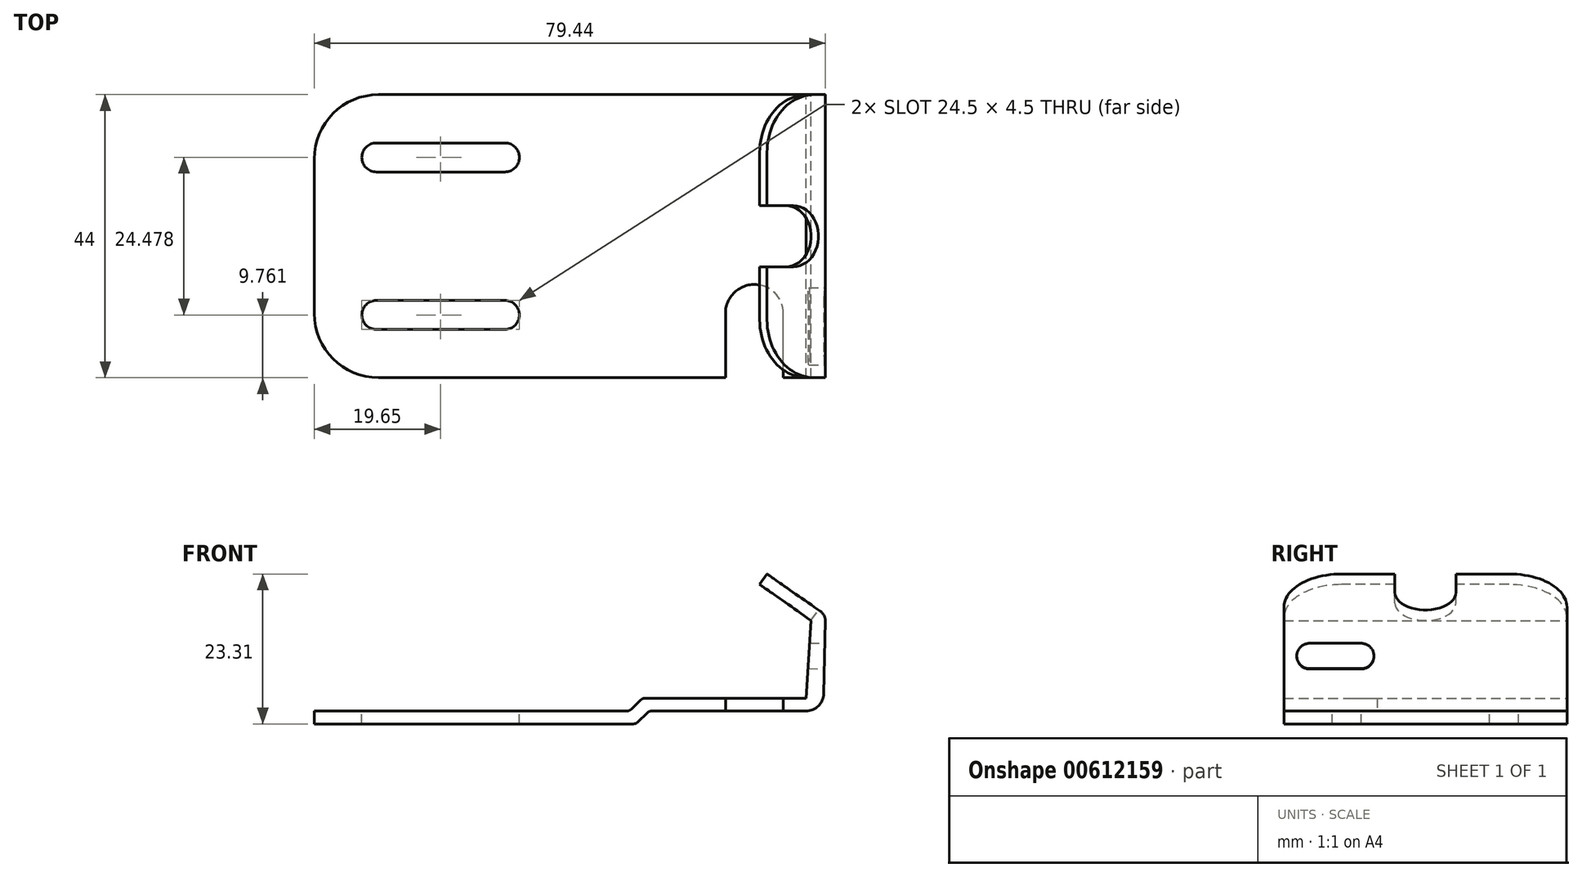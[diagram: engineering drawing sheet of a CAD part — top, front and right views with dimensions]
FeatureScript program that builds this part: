
annotation { "Feature Type Name" : "Feature", "Feature Type Description" : "" }
export const myFeature = defineFeature(function(context is Context, id is Id, definition is map)
    precondition{}
    {
        {
            var Q0;
            Q0=qCreatedBy(makeId("Front.planeOp"),FACE);
            var sketch = newSketch(context, id + "F0", { "sketchPlane" : qUnion([Q0])});
            skLineSegment(sketch, "E0", {"start": v(-0.4, 0) * mm, "end": v(-40, 0) * mm});
            skLineSegment(sketch, "E1", {"start": v(-40, 0) * mm, "end": v(-40, 2) * mm});
            skLineSegment(sketch, "E2", {"start": v(-40, 2) * mm, "end": v(-1.43, 2) * mm});
            skLineSegment(sketch, "E3", {"start": v(-0.73, 2.28) * mm, "end": v(0.75, 3.72) * mm});
            skLineSegment(sketch, "E4", {"start": v(1.44, 4) * mm, "end": v(26.44, 4) * mm});
            skLineSegment(sketch, "E5", {"start": v(0.3, 0.28) * mm, "end": v(1.77, 1.72) * mm});
            skLineSegment(sketch, "E6", {"start": v(2.46, 2) * mm, "end": v(26.44, 2) * mm});
            skPoint(sketch, "E7.visualSharp", {"position": v(-1.02, 2) * mm});
            skArc(sketch, "E7.filletArc", {"start": v(-1.43, 2) * mm, "mid": v(-1.05, 2.07) * mm, "end": v(-0.73, 2.28) * mm});
            skPoint(sketch, "E8.visualSharp", {"position": v(1.04, 4) * mm});
            skArc(sketch, "E8.filletArc", {"start": v(1.44, 4) * mm, "mid": v(1.07, 3.93) * mm, "end": v(0.75, 3.72) * mm});
            skPoint(sketch, "E9.visualSharp", {"position": v(2.06, 2) * mm});
            skArc(sketch, "E9.filletArc", {"start": v(2.46, 2) * mm, "mid": v(2.09, 1.93) * mm, "end": v(1.77, 1.72) * mm});
            skPoint(sketch, "E10.visualSharp", {"position": v(0, 0) * mm});
            skArc(sketch, "E10.filletArc", {"start": v(-0.4, 0) * mm, "mid": v(-0.03, 0.07) * mm, "end": v(0.3, 0.28) * mm});
            skArc(sketch, "E11", {"start": v(26.44, 2) * mm, "mid": v(28.38, 2.79) * mm, "end": v(29.2, 4.7) * mm});
            skLineSegment(sketch, "E12", {"start": v(29.2, 4.7) * mm, "end": v(29.44, 16.03) * mm});
            skArc(sketch, "E13", {"start": v(29.44, 16.03) * mm, "mid": v(29.26, 16.85) * mm, "end": v(28.7, 17.5) * mm});
            skLineSegment(sketch, "E14", {"start": v(28.7, 17.5) * mm, "end": v(27.76, 18.15) * mm});
            skLineSegment(sketch, "E15", {"start": v(27.76, 18.15) * mm, "end": v(26.61, 16.51) * mm});
            skLineSegment(sketch, "E16", {"start": v(26.61, 16.51) * mm, "end": v(27.25, 16.06) * mm});
            skLineSegment(sketch, "E17", {"start": v(27.25, 16.06) * mm, "end": v(26.44, 4) * mm});
            skSolve(sketch);
        }
        {
            var Q0;
            Q0=makeQuery(id+"F0.imprint","IMPRINT",FACE,{"disambiguationData":[TD([[makeQuery(id+"F0.imprint","IMPRINT",EDGE,{"derivedFrom":sQuery(id+"F0.wireOp",EDGE,"E0")}),-1.0]])]});
            extrude(context, id + "F1", {"entities" : qUnion([Q0]), "endBound" : BoundingType.SYMMETRIC, "depth" : 44 * mm, "offsetDistance" : 25 * mm});
        }
        {
            var Q0;
            Q0=makeQuery(id+"F1.opExtrude","SWEPT_FACE",FACE,{"disambiguationData":[OSD([sQuery(id+"F0.wireOp",EDGE,"E2")])]});
            var sketch = newSketch(context, id + "F2", { "sketchPlane" : qUnion([Q0])});
            skLineSegment(sketch, "E18", {"start": v(-50, -12) * mm, "end": v(-50, 12) * mm});
            skArc(sketch, "E19", {"start": v(-50, -12) * mm, "mid": v(-47.07, -19.07) * mm, "end": v(-40, -22) * mm});
            skArc(sketch, "E20", {"start": v(-50, 12) * mm, "mid": v(-47.07, 19.07) * mm, "end": v(-40, 22) * mm});
            skSolve(sketch);
        }
        {
            var Q0;
            Q0=makeQuery(id+"F2.imprint","IMPRINT",FACE,{"disambiguationData":[TD([[makeQuery(id+"F2.imprint","IMPRINT",EDGE,{"derivedFrom":sQuery(id+"F2.wireOp",EDGE,"E18")}),-1.0]])]});
            extrude(context, id + "F3", {"entities" : qUnion([Q0]), "operationType" : NewBodyOperationType.ADD, "oppositeDirection" : true, "depth" : 2 * mm, "offsetDistance" : 25 * mm});
        }
        {
            var Q0;
            {var subQ0=sQuery(id+"F0.wireOp",EDGE,"E2");Q0=makeQuery(id+"F3.boolean.opBoolean","MERGE",FACE,{"derivedFrom":[makeQuery(id+"F1.opExtrude","SWEPT_FACE",FACE,{"disambiguationData":[OSD([subQ0])]}),makeQuery(id+"F3.opExtrude","CAP_FACE",FACE,{"disambiguationData":[OSD([sQuery(id+"F0.wireOp",EDGE,"E1"),subQ0,sQuery(id+"F2.wireOp",EDGE,"E18"),sQuery(id+"F2.wireOp",EDGE,"E19"),sQuery(id+"F2.wireOp",EDGE,"E20")])],"isStart":true})]});}
            var sketch = newSketch(context, id + "F4", { "sketchPlane" : qUnion([Q0])});
            skLineSegment(sketch, "E21.bottom", {"start": v(-40.35, 9.99) * mm, "end": v(-20.35, 9.99) * mm});
            skLineSegment(sketch, "E21.top", {"start": v(-40.35, 14.49) * mm, "end": v(-20.35, 14.49) * mm});
            skArc(sketch, "E22", {"start": v(-40.35, 14.49) * mm, "mid": v(-42.6, 12.24) * mm, "end": v(-40.35, 9.99) * mm});
            skArc(sketch, "E23", {"start": v(-20.35, 9.99) * mm, "mid": v(-18.1, 12.24) * mm, "end": v(-20.35, 14.49) * mm});
            skLineSegment(sketch, "E24.MirrorCS", {"start": v(-40.35, -9.99) * mm, "end": v(-20.35, -9.99) * mm});
            skArc(sketch, "E25.MirrorCS", {"start": v(-40.35, -14.49) * mm, "mid": v(-42.6, -12.24) * mm, "end": v(-40.35, -9.99) * mm});
            skLineSegment(sketch, "E26.MirrorCS", {"start": v(-40.35, -14.49) * mm, "end": v(-20.35, -14.49) * mm});
            skArc(sketch, "E27.MirrorCS", {"start": v(-20.35, -9.99) * mm, "mid": v(-18.1, -12.24) * mm, "end": v(-20.35, -14.49) * mm});
            skSolve(sketch);
        }
        {
            var Q0;
            Q0 = qSketchRegion(id + "F4", true);
            var Q1;
            Q1=makeQuery(id+"F3.boolean.opBoolean","MERGE",FACE,{"derivedFrom":[makeQuery(id+"F1.opExtrude","SWEPT_FACE",FACE,{"disambiguationData":[OSD([sQuery(id+"F0.wireOp",EDGE,"E0")])]}),makeQuery(id+"F3.opExtrude","CAP_FACE",FACE,{"disambiguationData":[OSD([sQuery(id+"F0.wireOp",EDGE,"E1"),sQuery(id+"F0.wireOp",EDGE,"E2"),sQuery(id+"F2.wireOp",EDGE,"E18"),sQuery(id+"F2.wireOp",EDGE,"E19"),sQuery(id+"F2.wireOp",EDGE,"E20")])],"isStart":false})]});
            extrude(context, id + "F5", {"entities" : qUnion([Q0]), "operationType" : NewBodyOperationType.REMOVE, "endBound" : BoundingType.UP_TO_SURFACE, "oppositeDirection" : true, "depth" : 25 * mm, "endBoundEntityFace" : qUnion([Q1]), "offsetDistance" : 25 * mm});
        }
        {
            var Q0;
            Q0=makeQuery(id+"F1.opExtrude","SWEPT_FACE",FACE,{"disambiguationData":[OSD([sQuery(id+"F0.wireOp",EDGE,"E12")])]});
            var sketch = newSketch(context, id + "F6", { "sketchPlane" : qUnion([Q0])});
            skLineSegment(sketch, "E28.bottom", {"start": v(-18, 13.15) * mm, "end": v(-10, 13.15) * mm});
            skLineSegment(sketch, "E28.top", {"start": v(-18, 9.15) * mm, "end": v(-10, 9.15) * mm});
            skArc(sketch, "E29", {"start": v(-10, 9.15) * mm, "mid": v(-8, 11.15) * mm, "end": v(-10, 13.15) * mm});
            skArc(sketch, "E30", {"start": v(-18, 13.15) * mm, "mid": v(-20, 11.15) * mm, "end": v(-18, 9.15) * mm});
            skSolve(sketch);
        }
        {
            var Q0;
            Q0 = qSketchRegion(id + "F6", true);
            var Q1;
            Q1=makeQuery(id+"F1.opExtrude","SWEPT_FACE",FACE,{"disambiguationData":[OSD([sQuery(id+"F0.wireOp",EDGE,"E17")])]});
            extrude(context, id + "F7", {"entities" : qUnion([Q0]), "operationType" : NewBodyOperationType.REMOVE, "endBound" : BoundingType.UP_TO_SURFACE, "oppositeDirection" : true, "depth" : 25 * mm, "endBoundEntityFace" : qUnion([Q1]), "offsetDistance" : 25 * mm});
        }
        {
            var Q0;
            Q0=makeQuery(id+"F1.opExtrude","SWEPT_FACE",FACE,{"disambiguationData":[OSD([sQuery(id+"F0.wireOp",EDGE,"E14")])]});
            var sketch = newSketch(context, id + "F8", { "sketchPlane" : qUnion([Q0])});
            skLineSegment(sketch, "E31", {"start": v(3.33, -13) * mm, "end": v(3.33, 13) * mm});
            skArc(sketch, "E32", {"start": v(3.33, -13) * mm, "mid": v(5.97, -19.36) * mm, "end": v(12.33, -22) * mm});
            skArc(sketch, "E33", {"start": v(3.33, 13) * mm, "mid": v(5.97, 19.36) * mm, "end": v(12.33, 22) * mm});
            skSolve(sketch);
        }
        {
            var Q0;
            Q0=makeQuery(id+"F8.imprint","IMPRINT",FACE,{"disambiguationData":[TD([[makeQuery(id+"F8.imprint","IMPRINT",EDGE,{"derivedFrom":sQuery(id+"F8.wireOp",EDGE,"E31")}),-1.0]])]});
            var Q1;
            Q1=makeQuery(id+"F1.opExtrude","SWEPT_FACE",FACE,{"disambiguationData":[OSD([sQuery(id+"F0.wireOp",EDGE,"E16")])]});
            extrude(context, id + "F9", {"entities" : qUnion([Q0]), "operationType" : NewBodyOperationType.ADD, "endBound" : BoundingType.UP_TO_SURFACE, "oppositeDirection" : true, "depth" : 25 * mm, "endBoundEntityFace" : qUnion([Q1]), "offsetDistance" : 25 * mm});
        }
        {
            var Q0;
            {var subQ0=sQuery(id+"F0.wireOp",EDGE,"E14");Q0=makeQuery(id+"F9.boolean.opBoolean","MERGE",FACE,{"derivedFrom":[makeQuery(id+"F1.opExtrude","SWEPT_FACE",FACE,{"disambiguationData":[OSD([subQ0])]}),makeQuery(id+"F9.opExtrude","CAP_FACE",FACE,{"disambiguationData":[OSD([subQ0,sQuery(id+"F0.wireOp",EDGE,"E15"),sQuery(id+"F8.wireOp",EDGE,"E31"),sQuery(id+"F8.wireOp",EDGE,"E32"),sQuery(id+"F8.wireOp",EDGE,"E33")])],"isStart":true})]});}
            var sketch = newSketch(context, id + "F10", { "sketchPlane" : qUnion([Q0])});
            skLineSegment(sketch, "E34", {"start": v(3.33, 0) * mm, "end": v(13.48, 0) * mm, "construction": true});
            skLineSegment(sketch, "E35", {"start": v(3.33, -4.75) * mm, "end": v(8.33, -4.75) * mm});
            skLineSegment(sketch, "E36", {"start": v(3.33, 4.75) * mm, "end": v(8.33, 4.75) * mm});
            skArc(sketch, "E37", {"start": v(8.33, -4.75) * mm, "mid": v(13.08, 0) * mm, "end": v(8.33, 4.75) * mm});
            skSolve(sketch);
        }
        {
            var Q0;
            {var subQ0=sQuery(id+"F10.wireOp",EDGE,"E35");Q0=makeQuery(id+"F10.imprint","IMPRINT",FACE,{"disambiguationData":[TD([[makeQuery(id+"F10.imprint","IMPRINT",EDGE,{"derivedFrom":subQ0}),1.0]])]});}
            var Q1;
            Q1=makeQuery(id+"F9.boolean.opBoolean","MERGE",FACE,{"derivedFrom":[makeQuery(id+"F1.opExtrude","SWEPT_FACE",FACE,{"disambiguationData":[OSD([sQuery(id+"F0.wireOp",EDGE,"E16")])]}),makeQuery(id+"F9.opExtrude","CAP_FACE",FACE,{"disambiguationData":[OSD([sQuery(id+"F0.wireOp",EDGE,"E14"),sQuery(id+"F0.wireOp",EDGE,"E15"),sQuery(id+"F8.wireOp",EDGE,"E31"),sQuery(id+"F8.wireOp",EDGE,"E32"),sQuery(id+"F8.wireOp",EDGE,"E33")])],"isStart":false})]});
            extrude(context, id + "F11", {"entities" : qUnion([Q0]), "operationType" : NewBodyOperationType.REMOVE, "endBound" : BoundingType.UP_TO_SURFACE, "oppositeDirection" : true, "depth" : 25 * mm, "endBoundEntityFace" : qUnion([Q1]), "offsetDistance" : 25 * mm});
        }
        {
            var Q0;
            Q0=makeQuery(id+"F1.opExtrude","SWEPT_FACE",FACE,{"disambiguationData":[OSD([sQuery(id+"F0.wireOp",EDGE,"E6")])]});
            var sketch = newSketch(context, id + "F12", { "sketchPlane" : qUnion([Q0])});
            skLineSegment(sketch, "E38.bottom", {"start": v(22.92, 22) * mm, "end": v(13.92, 22) * mm});
            skLineSegment(sketch, "E38.left", {"start": v(22.92, 22) * mm, "end": v(22.92, 12) * mm});
            skLineSegment(sketch, "E38.right", {"start": v(13.92, 22) * mm, "end": v(13.92, 12) * mm});
            skArc(sketch, "E39", {"start": v(13.92, 12) * mm, "mid": v(18.42, 7.5) * mm, "end": v(22.92, 12) * mm});
            skSolve(sketch);
        }
        {
            var Q0;
            Q0 = qSketchRegion(id + "F12", true);
            extrude(context, id + "F13", {"entities" : qUnion([Q0]), "operationType" : NewBodyOperationType.REMOVE, "endBound" : BoundingType.UP_TO_NEXT, "oppositeDirection" : true, "depth" : 25 * mm, "offsetDistance" : 25 * mm});
        }
    });
